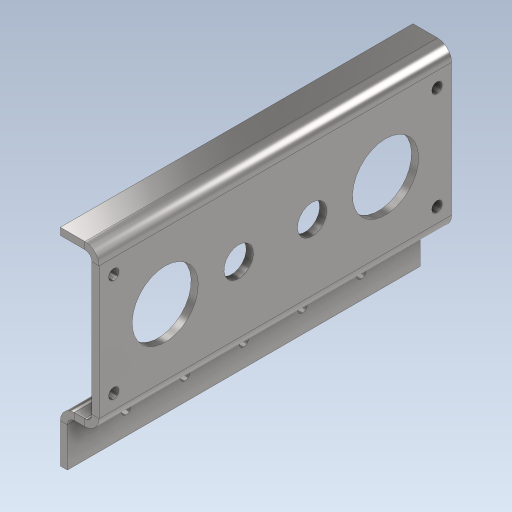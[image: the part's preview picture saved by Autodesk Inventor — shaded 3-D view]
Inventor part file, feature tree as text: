
AUTODESK INVENTOR PART (.ipt)
format: ipt  version: 2023 (Build 270158000, 158)  size: 230,400 bytes
history: native  units: in
note: dims shown in document units (in); Inventor stores cm internally (conversion verified against a paired STEP export)
features: sheet_metal_op x7, sketch x5, other x3, hole x2, projected_geometry x1
ambient origin geometry x8: Origin, YZ Plane, XZ Plane, XY Plane, X Axis, Y Axis, Z Axis, Center Point
bodies: Body1 (feature_tree)
feature tree (18):
  sheet_metal_op  "Face2"
  sheet_metal_op  "Flange1"
  sheet_metal_op  "Flange2"
  hole  "Hole2"  [1 undecoded]
  hole  "Hole1"  [1 undecoded]
  sketch  "Sketch1"  dims[d0=2.25in d1=6.0in]
  other  "Plate2"
  sketch  "Sketch2"  dims[d2=1.25in d3=1.25in]
  other  "Plate3"
  sheet_metal_op  "Bend1"
  sheet_metal_op  "Corner1"
  sketch  "Sketch3"  dims[d4=1.25in]
  projected_geometry  "Projected Loop1"
  sketch  "Sketch4"  dims[d6=1.125in]
  other  "Plate4"
  sheet_metal_op  "Bend2"
  sheet_metal_op  "Corner2"
  sketch  "Sketch5"  dims[d7=0.5in d8=1.125in d10=0.12in d11=0.177in d12=5.5in d13=1.75in d14=0.5in d15=6.0in d16=0.5in d17=6.0in d18=0.12in d19=0.06in d20=0.24in d21=0.12in d22=0.6583in d23=90.0deg d24=0.12in d25=0.48in d26=0.12in d27=0.12in d28=1.0in d29=1.9685in d31=1.0in d32=0.3937in d34=1.0in d36=0.1628in d37=5.0in d38=0.375in d39=0.25in d40=0.5635in d41=0.12in d42=0.8108in d43=0.12in d44=0.06in d45=0.24in d46=0.12in d47=0.7874in d48=90.0deg d49=0.12in d50=0.48in d51=0.12in d52=0.12in d53=1.0in d54=0.3937in d55=1.9685in d57=1.0in d58=0.3937in d60=1.0in d62=0.1628in d63=0.394in d64=0.375in d65=0.25in d66=0.5635in d67=1.0in d68=0.8108in]
note: 2 required parameter values undecoded (feature->parameter linkage not recoverable at this tier; creation-order binding heuristic only, values carry confidence <= 0.55)
